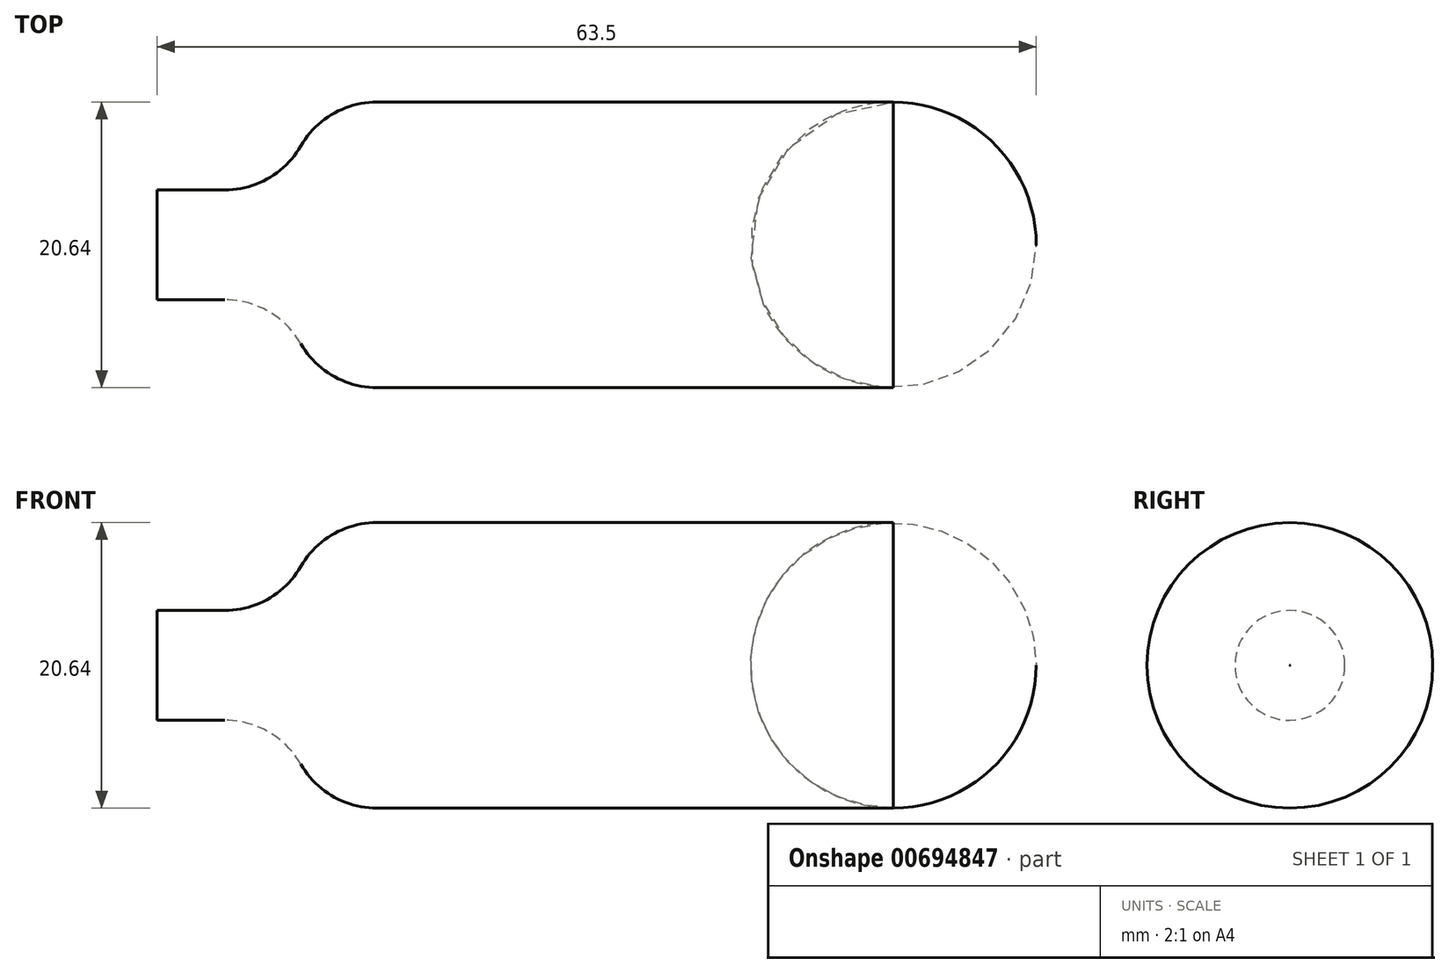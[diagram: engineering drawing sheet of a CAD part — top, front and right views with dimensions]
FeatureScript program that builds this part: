
annotation { "Feature Type Name" : "Feature", "Feature Type Description" : "" }
export const myFeature = defineFeature(function(context is Context, id is Id, definition is map)
    precondition{}
    {
        {
            var Q0;
            Q0=qCreatedBy(makeId("Front.planeOp"),FACE);
            var sketch = newSketch(context, id + "F0", { "sketchPlane" : qUnion([Q0])});
            skLineSegment(sketch, "E0", {"start": v(0, 0) * mm, "end": v(63.5, 0) * mm});
            skLineSegment(sketch, "E1", {"start": v(0, 0) * mm, "end": v(0, 3.97) * mm});
            skLineSegment(sketch, "E2", {"start": v(0, 3.97) * mm, "end": v(3.18, 3.97) * mm});
            skLineSegment(sketch, "E3", {"start": v(15.88, 10.32) * mm, "end": v(53.19, 10.32) * mm});
            skPoint(sketch, "E4.visualSharp", {"position": v(9.53, 3.97) * mm});
            skLineSegment(sketch, "E5", {"start": v(3.18, 3.97) * mm, "end": v(4.88, 3.97) * mm});
            skPoint(sketch, "E6.visualSharp", {"position": v(9.53, 10.32) * mm});
            skArc(sketch, "E6.filletArc", {"start": v(15.88, 10.32) * mm, "mid": v(12.7, 9.47) * mm, "end": v(10.38, 7.14) * mm});
            skPoint(sketch, "E7.visualSharp", {"position": v(9.52, 3.97) * mm});
            skArc(sketch, "E7.filletArc", {"start": v(4.88, 3.97) * mm, "mid": v(8.05, 4.82) * mm, "end": v(10.38, 7.14) * mm});
            skLineSegment(sketch, "E8", {"start": v(63.5, 0) * mm, "end": v(63.5, 0) * mm});
            skPoint(sketch, "E9.visualSharp", {"position": v(63.5, 10.32) * mm});
            skArc(sketch, "E9.filletArc", {"start": v(63.5, 0) * mm, "mid": v(60.48, 7.3) * mm, "end": v(53.19, 10.32) * mm});
            skSolve(sketch);
        }
        {
            var Q0;
            Q0=makeQuery(id+"F0.imprint","IMPRINT",FACE,{"disambiguationData":[TD([[makeQuery(id+"F0.imprint","IMPRINT",EDGE,{"derivedFrom":sQuery(id+"F0.wireOp",EDGE,"E0")}),1.0]])]});
            var Q1;
            Q1=sQuery(id+"F0.wireOp",EDGE,"E0");
            revolve(context, id + "F1", {"entities" : qUnion([Q0]), "axis" : qUnion([Q1]), "revolveType" : RevolveType.FULL});
        }
    });
